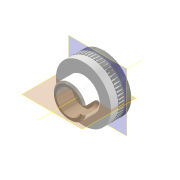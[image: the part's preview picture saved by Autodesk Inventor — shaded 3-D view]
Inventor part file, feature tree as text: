
AUTODESK INVENTOR PART (.ipt)
format: ipt  version: 2022 (Build 260153000, 153)  size: 752,640 bytes
history: native  units: mm
features: other x6, extrude x4, sketch x4, plane x2, projected_geometry x1
ambient origin geometry x8: Origin, YZ Plane, XZ Plane, XY Plane, X Axis, Y Axis, Z Axis, Center Point
bodies: Volumenkörper1 (feature_tree), Volumenkörper2 (feature_tree)
feature tree (17):
  other  "00_SM05FC2-Step.ipt"
  plane  "Arbeitsebene1"
  extrude  "Extrusion1"  [1 undecoded]
  plane  "Arbeitsebene2"
  extrude  "Extrusion2"  Depth=3.0mm TaperAngle=0.0deg
  extrude  "Extrusion3"  Depth=3.0mm
  extrude  "Extrusion4"  [1 undecoded]
  other  "Volumenkörper1::00_SM05FC2-Step.ipt"
  other  "Volumenkörper2::00_SM05FC2-Step.ipt"
  other  "Bezeichnung1"
  sketch  "Skizze1"  dims[d0=10.0mm d1=-0.5mm]
  other  "Arbeitsachse1"
  other  "Arbeitspunkt1"
  sketch  "Skizze3"  dims[d2=3.0mm d3=0.0mm d5=12.12mm d6=0.0mm]
  sketch  "Skizze4"  dims[d7=3.0mm d8=0.3mm d9=0.0mm d10=0.0mm d11=3.0mm]
  sketch  "Skizze5"  dims[d12=0.0mm d13=0.0mm]
  projected_geometry  "Projizierte Kontur1"
note: 2 required parameter values undecoded (feature->parameter linkage not recoverable at this tier; creation-order binding heuristic only, values carry confidence <= 0.55)
